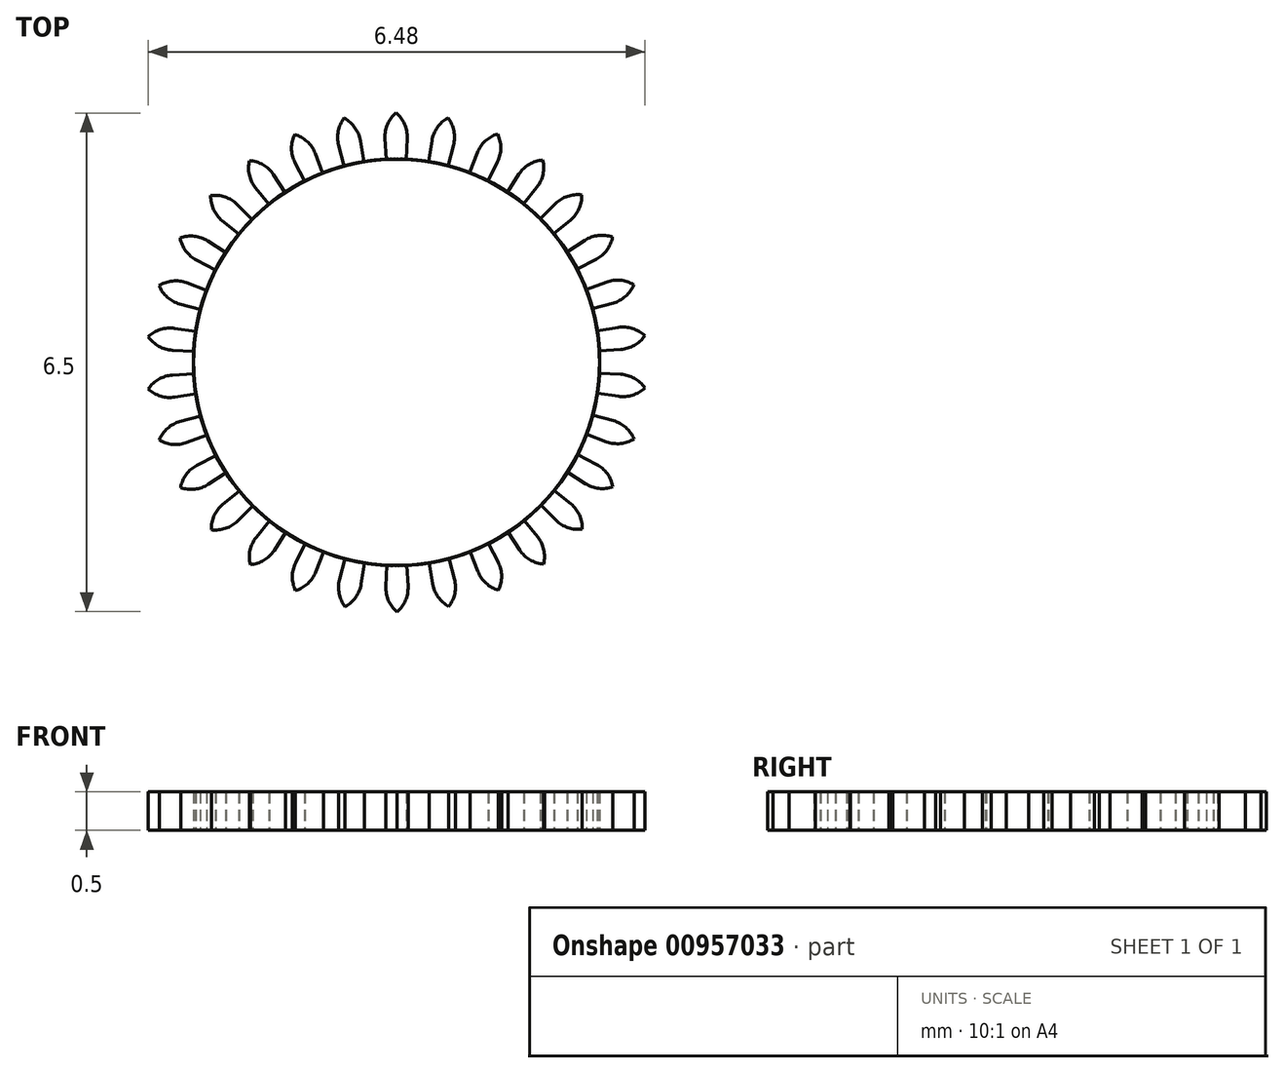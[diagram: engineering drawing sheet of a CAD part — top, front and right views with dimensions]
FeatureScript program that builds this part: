
annotation { "Feature Type Name" : "Feature", "Feature Type Description" : "" }
export const myFeature = defineFeature(function(context is Context, id is Id, definition is map)
    precondition{}
    {
        {
            var Q0;
            Q0=qCreatedBy(makeId("Top.planeOp"),FACE);
            var sketch = newSketch(context, id + "F0", { "sketchPlane" : qUnion([Q0])});
            skCircle(sketch, "E0", {"center": v(0, 0) * mm, "radius": 2.65 * mm});
            skCircle(sketch, "E1", {"center": v(0, 0) * mm, "radius": 3 * mm});
            skCircle(sketch, "E2", {"center": v(0, 0) * mm, "radius": 3.25 * mm});
            skLineSegment(sketch, "E3", {"start": v(0, 3.25) * mm, "end": v(0, 0) * mm});
            skLineSegment(sketch, "E4.0", {"start": v(-0.15, 3.25) * mm, "end": v(-0.15, 3.25) * mm});
            skLineSegment(sketch, "E5.0", {"start": v(0.13, 3.25) * mm, "end": v(0.13, 3.25) * mm});
            skPoint(sketch, "E6.first.point", {"position": v(0.14, 3) * mm});
            skPoint(sketch, "E6.third.point", {"position": v(-0.58, 2.68) * mm});
            skPoint(sketch, "E7.first.point", {"position": v(-0.15, 3) * mm});
            skPoint(sketch, "E7.third.point", {"position": v(0.55, 2.66) * mm});
            skLineSegment(sketch, "E8", {"start": v(-0.14, 2.65) * mm, "end": v(-0.15, 2.92) * mm});
            skArc(sketch, "E9.trimOffspring", {"start": v(0, 3.25) * mm, "mid": v(-0.12, 3.1) * mm, "end": v(-0.15, 2.92) * mm});
            skArc(sketch, "E10.MirrorCS", {"start": v(0, 3.25) * mm, "mid": v(0.1, 3.1) * mm, "end": v(0.14, 2.92) * mm});
            skLineSegment(sketch, "E11.MirrorCS", {"start": v(0.13, 2.65) * mm, "end": v(0.14, 2.92) * mm});
            skPoint(sketch, "E12.1.0", {"position": v(1.5, 2.26) * mm});
            skPoint(sketch, "E12.2.0", {"position": v(2.24, 1.53) * mm});
            skLineSegment(sketch, "E12.anchor1", {"start": v(0, 0) * mm, "end": v(0.55, 2.66) * mm, "construction": true});
            skLineSegment(sketch, "E12.anchor2", {"start": v(0, 0) * mm, "end": v(2.24, 1.53) * mm, "construction": true});
            skPoint(sketch, "E13.2.0", {"position": v(2.65, 0.58) * mm});
            skLineSegment(sketch, "E13.anchor1", {"start": v(0, 0) * mm, "end": v(1.5, 2.26) * mm, "construction": true});
            skLineSegment(sketch, "E13.anchor2", {"start": v(0, 0) * mm, "end": v(2.65, 0.58) * mm, "construction": true});
            skPoint(sketch, "E14.1.0", {"position": v(2.03, -1.8) * mm});
            skLineSegment(sketch, "E14.1.1", {"start": v(0, 0) * mm, "end": v(2.03, -1.8) * mm, "construction": true});
            skPoint(sketch, "E14.2.0", {"position": v(-2.58, -0.86) * mm});
            skLineSegment(sketch, "E14.2.1", {"start": v(0, 0) * mm, "end": v(-2.58, -0.86) * mm, "construction": true});
            skLineSegment(sketch, "E14.anchor2", {"start": v(0, 0) * mm, "end": v(-2.58, -0.86) * mm, "construction": true});
            skArc(sketch, "E15.MirrorCS", {"start": v(1.3, 2.99) * mm, "mid": v(1.33, 2.8) * mm, "end": v(1.3, 2.63) * mm});
            skArc(sketch, "E16.MirrorCS", {"start": v(1.3, 2.99) * mm, "mid": v(1.13, 2.9) * mm, "end": v(1.03, 2.74) * mm});
            skLineSegment(sketch, "E17.MirrorCS", {"start": v(0.93, 2.48) * mm, "end": v(1.03, 2.74) * mm});
            skLineSegment(sketch, "E18.MirrorCS", {"start": v(1.17, 2.38) * mm, "end": v(1.3, 2.63) * mm});
            skSolve(sketch);
        }
        {
            var Q0;
            {var subQ0=sQuery(id+"F0.wireOp",EDGE,"E0");var subQ5=makeQuery(id+"F0.imprint","INTERSECT",VERTEX,{"derivedFrom":[subQ0,sQuery(id+"F0.wireOp",EDGE,"E18.MirrorCS")]});Q0=makeQuery(id+"F0.imprint","IMPRINT",FACE,{"disambiguationData":[TD([[makeQuery(id+"F0.imprint","IMPRINT",EDGE,{"disambiguationData":[TD([[subQ5,-1.0]])],"derivedFrom":subQ0}),1.0]])]});}
            var Q1;
            {var subQ0=sQuery(id+"F0.wireOp",EDGE,"E11.MirrorCS");Q1=makeQuery(id+"F0.imprint","IMPRINT",FACE,{"disambiguationData":[TD([[makeQuery(id+"F0.imprint","IMPRINT",EDGE,{"derivedFrom":subQ0}),1.0]])]});}
            var Q2;
            {var subQ1=sQuery(id+"F0.wireOp",EDGE,"E3");var subQ3=sQuery(id+"F0.wireOp",EDGE,"E1");var subQ4=makeQuery(id+"F0.imprint","INTERSECT",VERTEX,{"derivedFrom":[subQ1,subQ3]});Q2=makeQuery(id+"F0.imprint","IMPRINT",FACE,{"disambiguationData":[TD([[makeQuery(id+"F0.imprint","IMPRINT",EDGE,{"disambiguationData":[TD([[subQ4,-1.0]])],"derivedFrom":subQ3}),-1.0]])]});}
            var Q3;
            {var subQ1=sQuery(id+"F0.wireOp",EDGE,"E3");var subQ3=sQuery(id+"F0.wireOp",EDGE,"E1");var subQ4=makeQuery(id+"F0.imprint","INTERSECT",VERTEX,{"derivedFrom":[subQ1,subQ3]});Q3=makeQuery(id+"F0.imprint","IMPRINT",FACE,{"disambiguationData":[TD([[makeQuery(id+"F0.imprint","IMPRINT",EDGE,{"disambiguationData":[TD([[subQ4,1.0]])],"derivedFrom":subQ3}),-1.0]])]});}
            var Q4;
            {var subQ0=sQuery(id+"F0.wireOp",EDGE,"E8");Q4=makeQuery(id+"F0.imprint","IMPRINT",FACE,{"disambiguationData":[TD([[makeQuery(id+"F0.imprint","IMPRINT",EDGE,{"derivedFrom":subQ0}),-1.0]])]});}
            extrude(context, id + "F1", {"entities" : qUnion([Q0, Q1, Q2, Q3, Q4]), "depth" : .5 * mm, "offsetDistance" : 25 * mm});
        }
        {
            var Q0;
            Q0=makeQuery(id+"F1.opExtrude","SWEPT_BODY",BODY,{"disambiguationData":[OSD([sQuery(id+"F0.wireOp",EDGE,"E0"),sQuery(id+"F0.wireOp",EDGE,"E8"),sQuery(id+"F0.wireOp",EDGE,"E9.trimOffspring"),sQuery(id+"F0.wireOp",EDGE,"E10.MirrorCS"),sQuery(id+"F0.wireOp",EDGE,"E11.MirrorCS")])]});
            var Q1;
            Q1=makeQuery(id+"F1.opExtrude","SWEPT_FACE",FACE,{"disambiguationData":[OSD([sQuery(id+"F0.wireOp",EDGE,"E0")])]});
            circularPattern(context, id + "F2", {"entities" : qUnion([Q0]), "axis" : qUnion([Q1]), "angle" : 360 * degree, "instanceCount" : 30, "equalSpace" : true});
        }
    });
